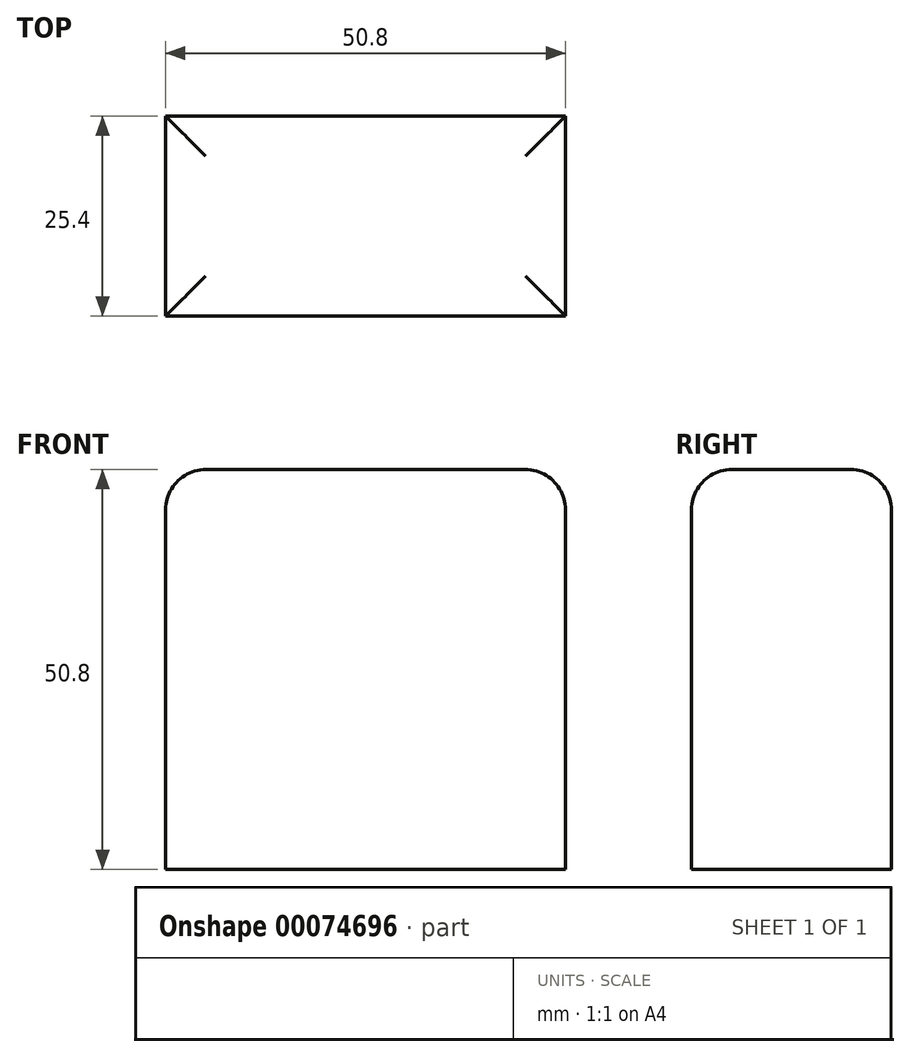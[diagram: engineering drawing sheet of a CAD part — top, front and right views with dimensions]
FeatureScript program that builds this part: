
annotation { "Feature Type Name" : "Feature", "Feature Type Description" : "" }
export const myFeature = defineFeature(function(context is Context, id is Id, definition is map)
    precondition{}
    {
        {
            var Q0;
            Q0=qCreatedBy(makeId("Front.planeOp"),FACE);
            var sketch = newSketch(context, id + "F0", { "sketchPlane" : qUnion([Q0])});
            skLineSegment(sketch, "E0.rect.bottom", {"start": v(25.4, -25.4) * mm, "end": v(-25.4, -25.4) * mm});
            skLineSegment(sketch, "E0.rect.top", {"start": v(25.4, 25.4) * mm, "end": v(-25.4, 25.4) * mm});
            skLineSegment(sketch, "E0.rect.left", {"start": v(25.4, -25.4) * mm, "end": v(25.4, 25.4) * mm});
            skLineSegment(sketch, "E0.rect.right", {"start": v(-25.4, -25.4) * mm, "end": v(-25.4, 25.4) * mm});
            skPoint(sketch, "E0.rect.middle", {"position": v(0, 0) * mm});
            skSolve(sketch);
        }
        {
            var Q0;
            Q0 = qSketchRegion(id + "F0", true);
            extrude(context, id + "F1", {"entities" : qUnion([Q0]), "endBound" : BoundingType.SYMMETRIC, "depth" : 25.4 * mm});
        }
        {
            var Q0;
            Q0=makeQuery(id+"F1.opExtrude","CAP_EDGE",EDGE,{"disambiguationData":[OSD([sQuery(id+"F0.wireOp",EDGE,"E0.rect.top")])],"isStart":false});
            var Q1;
            Q1=makeQuery(id+"F1.opExtrude","SWEPT_EDGE",EDGE,{"disambiguationData":[OSD([sQuery(id+"F0.wireOp",EDGE,"E0.rect.top"),sQuery(id+"F0.wireOp",EDGE,"E0.rect.left")])]});
            var Q2;
            Q2=makeQuery(id+"F1.opExtrude","CAP_EDGE",EDGE,{"disambiguationData":[OSD([sQuery(id+"F0.wireOp",EDGE,"E0.rect.top")])],"isStart":true});
            var Q3;
            Q3=makeQuery(id+"F1.opExtrude","SWEPT_EDGE",EDGE,{"disambiguationData":[OSD([sQuery(id+"F0.wireOp",EDGE,"E0.rect.top"),sQuery(id+"F0.wireOp",EDGE,"E0.rect.right")])]});
            fillet(context, id + "F2", {"entities" : qUnion([Q0, Q1, Q2, Q3]), "radius" : 5.08 * mm, "tangentPropagation" : true, "allowEdgeOverflow" : false});
        }
    });
